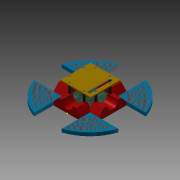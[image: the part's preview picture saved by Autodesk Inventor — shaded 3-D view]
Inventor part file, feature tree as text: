
AUTODESK INVENTOR PART (.ipt)
format: ipt  version: 2015 (Build 190159000, 159)  size: 516,608 bytes
history: native  units: in
note: dims shown in document units (in); Inventor stores cm internally (conversion verified against a paired STEP export)
features: sketch x10, extrude x9, pattern_circular x6, plane x3, mirror x2
ambient origin geometry x8: Origin, YZ Plane, XZ Plane, XY Plane, X Axis, Y Axis, Z Axis, Center Point
bodies: Solid1 (feature_tree)
feature tree (30):
  extrude  "Extrusion1"  Depth=0.1181in TaperAngle=0.0deg
  extrude  "Extrusion4"  Depth=1.5748in TaperAngle=360.0deg
  pattern_circular  "Circular Pattern2"  Count=4 Angle=360.0deg
  plane  "Work Plane1"
  extrude  "Extrusion6"  Depth=0.0787in
  sketch  "Sketch7"  dims[d30=0.1969in]
  pattern_circular  "Circular Pattern3"  Count=4 Angle=360.0deg
  plane  "Work Plane2"
  extrude  "Extrusion7"  Depth=1.063in
  mirror  "Mirror2"
  pattern_circular  "Circular Pattern4"  [2 undecoded]
  plane  "Work Plane3"
  extrude  "Extrusion8"  Depth=0.0394in TaperAngle=0.0deg
  extrude  "Extrusion9"  Depth=0.0394in TaperAngle=0.0deg
  extrude  "Extrusion10"  Depth=0.1181in TaperAngle=0.0deg
  pattern_circular  "Circular Pattern5"  Count=4 Angle=360.0deg
  extrude  "Extrusion11"  Depth=0.1181in TaperAngle=0.0deg
  pattern_circular  "Circular Pattern6"  Count=4 Angle=360.0deg
  extrude  "Extrusion12"  Depth=0.0394in TaperAngle=0.0deg
  mirror  "Mirror3"
  pattern_circular  "Circular Pattern7"  Count=4 Angle=360.0deg
  sketch  "Sketch1"  dims[d0=3.1496in d8=0.1181in d9=0.0in]
  sketch  "Sketch4"  dims[d19=0.3937in d20=0.0in d21=1.5748in d22=360.0deg]
  sketch  "Sketch6"  dims[d24=0.8071in]
  sketch  "Sketch8"  dims[d32=0.1181in]
  sketch  "Sketch9"  dims[d33=0.1181in]
  sketch  "Sketch10"  dims[d34=0.3937in d35=0.0in d36=1.5748in d37=360.0deg]
  sketch  "Sketch15"  dims[d39=0.315in d40=0.0787in]
  sketch  "Sketch16"  dims[d41=0.2756in d42=0.0in d43=1.5748in d44=360.0deg]
  sketch  "Sketch17"  dims[d46=0.2756in d47=1.063in d48=1.063in d49=0.0394in d50=0.0in d51=0.0394in d52=0.0in d58=0.1181in d59=0.0in d60=1.5748in d61=360.0deg d63=0.1181in d64=0.0in d65=1.5748in d66=360.0deg d68=0.0394in d69=0.0in d70=1.5748in d71=360.0deg]
note: 2 required parameter values undecoded (feature->parameter linkage not recoverable at this tier; creation-order binding heuristic only, values carry confidence <= 0.55)
